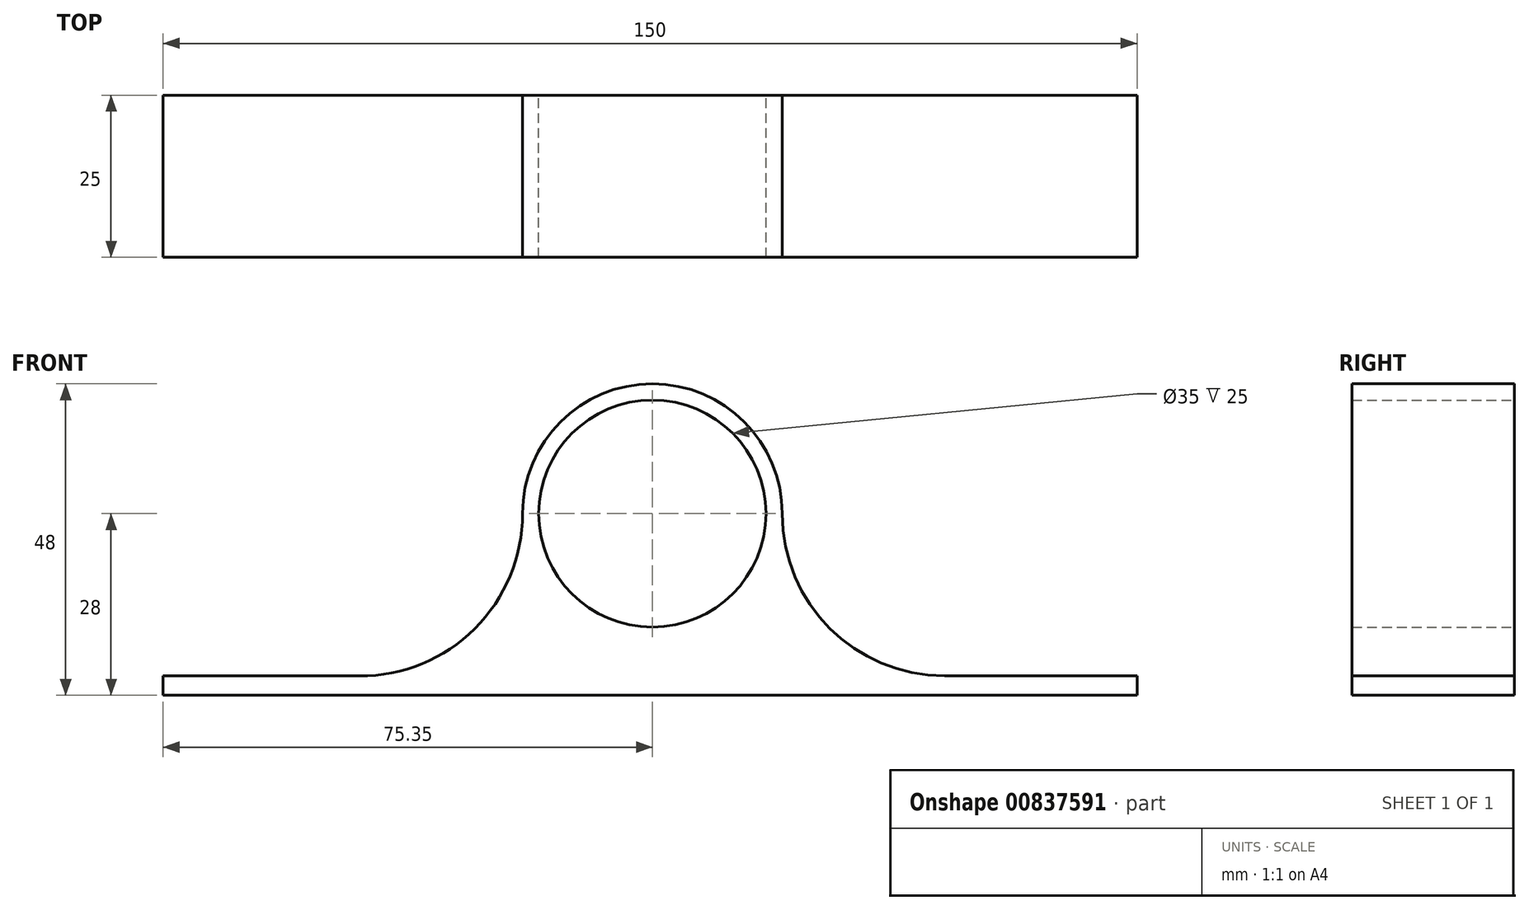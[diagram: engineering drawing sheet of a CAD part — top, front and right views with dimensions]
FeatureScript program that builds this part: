
annotation { "Feature Type Name" : "Feature", "Feature Type Description" : "" }
export const myFeature = defineFeature(function(context is Context, id is Id, definition is map)
    precondition{}
    {
        {
            var Q0;
            Q0=qCreatedBy(makeId("Front.planeOp"),FACE);
            var sketch = newSketch(context, id + "F0", { "sketchPlane" : qUnion([Q0])});
            skCircle(sketch, "E0", {"center": v(0, 0) * mm, "radius": 20 * mm});
            skLineSegment(sketch, "E1.bottom", {"start": v(-50.35, -25) * mm, "end": v(-75.35, -25) * mm});
            skPoint(sketch, "E1.middle", {"position": v(0, -30) * mm});
            skPoint(sketch, "E2.newPointB", {"position": v(74.65, -25) * mm});
            skLineSegment(sketch, "E3", {"start": v(50.35, -25) * mm, "end": v(75.35, -25) * mm});
            skCircle(sketch, "E4", {"center": v(0, 0) * mm, "radius": 17.5 * mm});
            skLineSegment(sketch, "E5", {"start": v(-20, 0) * mm, "end": v(-20, -0.02) * mm});
            skLineSegment(sketch, "E6", {"start": v(-45.1, -25.02) * mm, "end": v(-50.35, -25) * mm});
            skLineSegment(sketch, "E7", {"start": v(20, 0) * mm, "end": v(20, 0) * mm});
            skLineSegment(sketch, "E8", {"start": v(45, -25) * mm, "end": v(50.35, -25) * mm});
            skPoint(sketch, "E9.visualSharp", {"position": v(20, -25) * mm});
            skArc(sketch, "E9.filletArc", {"start": v(20, 0) * mm, "mid": v(27.32, -17.68) * mm, "end": v(45, -25) * mm});
            skPoint(sketch, "E10.visualSharp", {"position": v(-20, -25.12) * mm});
            skArc(sketch, "E10.filletArc", {"start": v(-45.1, -25.02) * mm, "mid": v(-27.36, -17.74) * mm, "end": v(-20, -0.02) * mm});
            skLineSegment(sketch, "E11", {"start": v(-75.35, -25) * mm, "end": v(-75.35, -28) * mm});
            skLineSegment(sketch, "E12", {"start": v(-75.35, -28) * mm, "end": v(74.65, -28) * mm});
            skLineSegment(sketch, "E13", {"start": v(74.65, -28) * mm, "end": v(74.65, -25) * mm});
            skSolve(sketch);
        }
        {
            var Q0;
            Q0=makeQuery(id+"F0.imprint","IMPRINT",FACE,{"disambiguationData":[TD([[makeQuery(id+"F0.imprint","IMPRINT",EDGE,{"derivedFrom":sQuery(id+"F0.wireOp",EDGE,"E1.bottom")}),1.0]])]});
            var Q1;
            Q1=makeQuery(id+"F0.imprint","IMPRINT",FACE,{"disambiguationData":[TD([[makeQuery(id+"F0.imprint","IMPRINT",EDGE,{"derivedFrom":sQuery(id+"F0.wireOp",EDGE,"E4")}),-1.0]])]});
            extrude(context, id + "F1", {"entities" : qUnion([Q0, Q1]), "depth" : 25 * mm, "offsetDistance" : 25 * mm});
        }
    });
